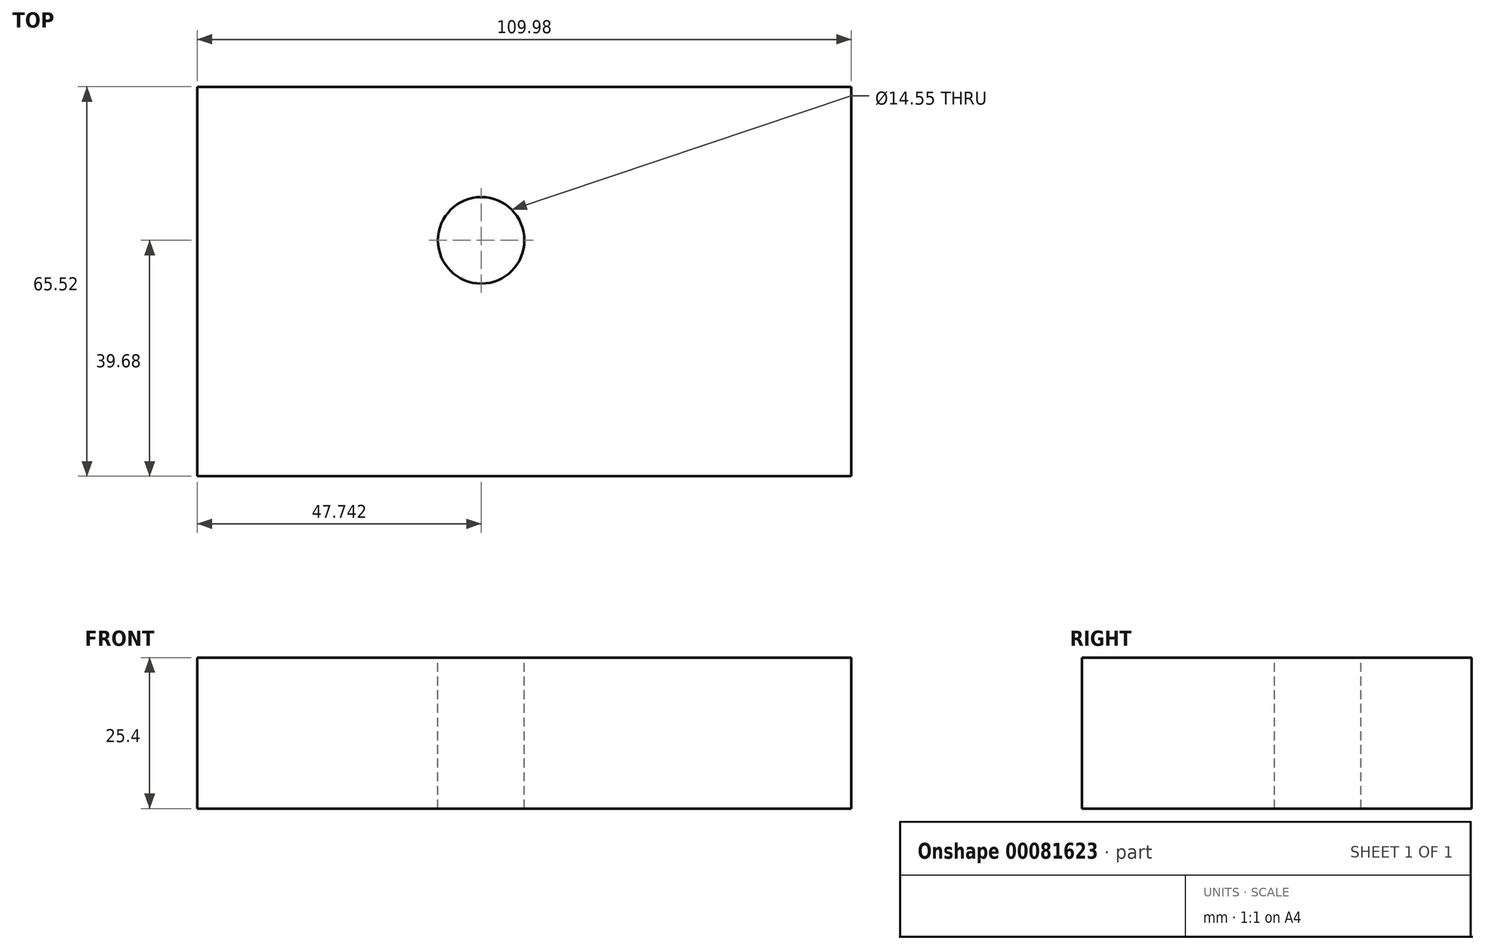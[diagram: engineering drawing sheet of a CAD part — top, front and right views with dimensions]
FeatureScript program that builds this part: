
annotation { "Feature Type Name" : "Feature", "Feature Type Description" : "" }
export const myFeature = defineFeature(function(context is Context, id is Id, definition is map)
    precondition{}
    {
        {
            var Q0;
            Q0=qCreatedBy(makeId("Top.planeOp"),FACE);
            var sketch = newSketch(context, id + "F0", { "sketchPlane" : qUnion([Q0])});
            skLineSegment(sketch, "E0.bottom", {"start": v(-42.15, 25.84) * mm, "end": v(67.83, 25.84) * mm});
            skLineSegment(sketch, "E0.top", {"start": v(-42.15, -39.68) * mm, "end": v(67.83, -39.68) * mm});
            skLineSegment(sketch, "E0.left", {"start": v(-42.15, 25.84) * mm, "end": v(-42.15, -39.68) * mm});
            skLineSegment(sketch, "E0.right", {"start": v(67.83, 25.84) * mm, "end": v(67.83, -39.68) * mm});
            skSolve(sketch);
        }
        {
            var Q0;
            Q0 = qSketchRegion(id + "F0", true);
            extrude(context, id + "F1", {"entities" : qUnion([Q0]), "depth" : 25.4 * mm});
        }
        {
            var Q0;
            Q0=makeQuery(id+"F1.opExtrude","CAP_FACE",FACE,{"disambiguationData":[OSD([sQuery(id+"F0.wireOp",EDGE,"E0.bottom"),sQuery(id+"F0.wireOp",EDGE,"E0.top"),sQuery(id+"F0.wireOp",EDGE,"E0.left"),sQuery(id+"F0.wireOp",EDGE,"E0.right")])],"isStart":false});
            var sketch = newSketch(context, id + "F2", { "sketchPlane" : qUnion([Q0])});
            skCircle(sketch, "E1", {"center": v(5.6, 0) * mm, "radius": 7.27 * mm});
            skSolve(sketch);
        }
        {
            var Q0;
            Q0 = qSketchRegion(id + "F2", true);
            extrude(context, id + "F3", {"entities" : qUnion([Q0]), "operationType" : NewBodyOperationType.REMOVE, "endBound" : BoundingType.UP_TO_NEXT, "oppositeDirection" : true, "depth" : 25.4 * mm});
        }
    });
